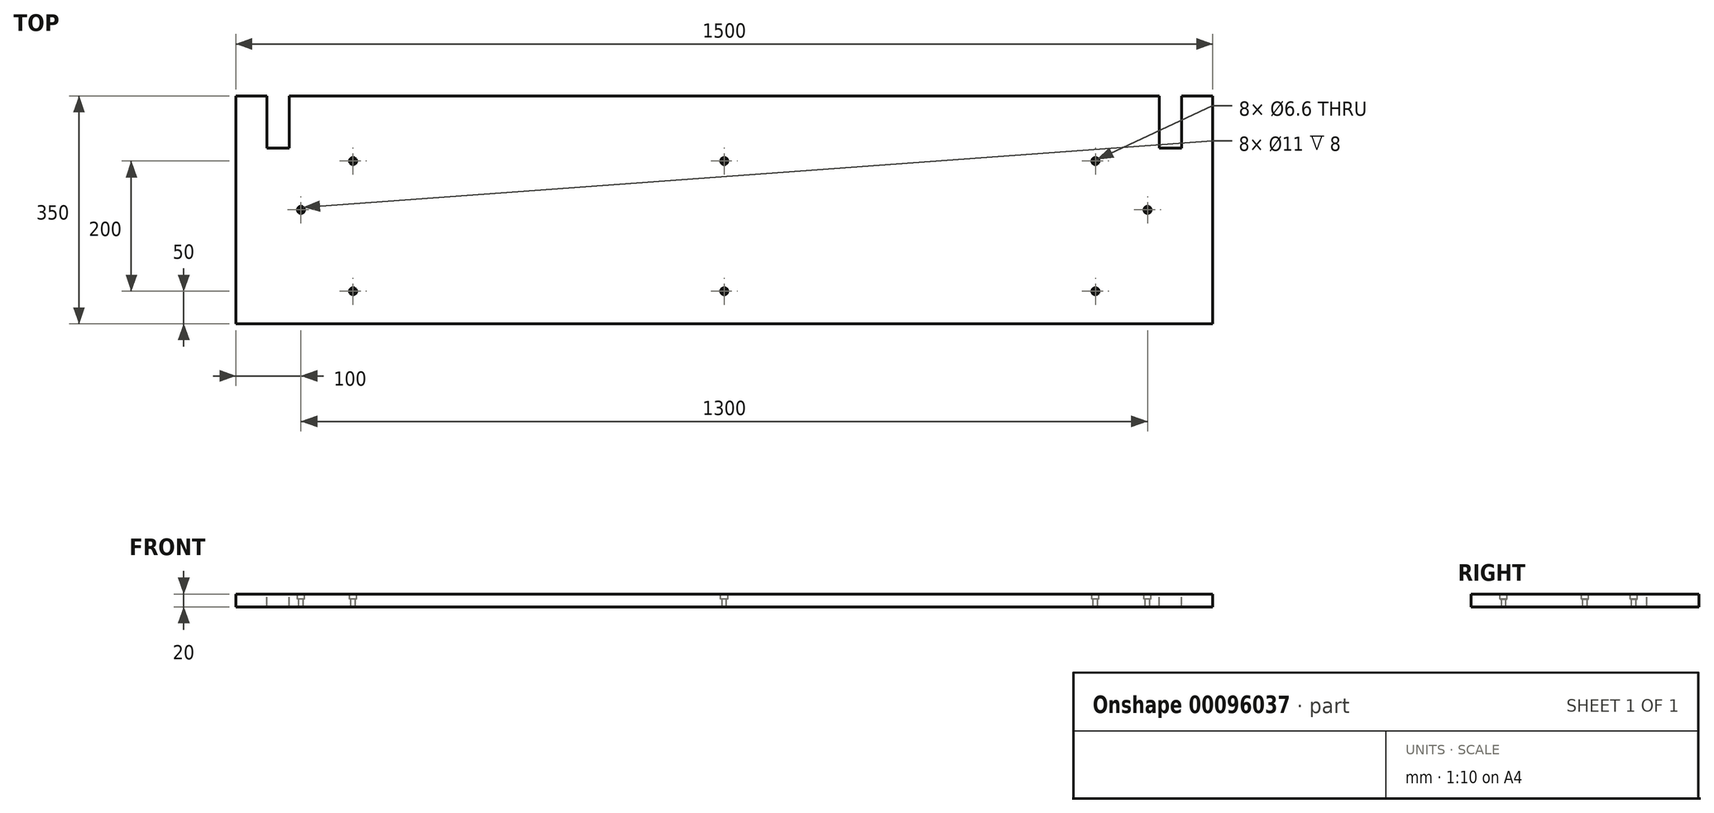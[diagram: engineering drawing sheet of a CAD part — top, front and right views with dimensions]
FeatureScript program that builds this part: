
annotation { "Feature Type Name" : "Feature", "Feature Type Description" : "" }
export const myFeature = defineFeature(function(context is Context, id is Id, definition is map)
    precondition{}
    {
        {
            var Q0;
            Q0=qCreatedBy(makeId("Top.planeOp"),FACE);
            var sketch = newSketch(context, id + "F0", { "sketchPlane" : qUnion([Q0])});
            skLineSegment(sketch, "E0.rect.bottom", {"start": v(750, -175) * mm, "end": v(-750, -175) * mm});
            skLineSegment(sketch, "E0.rect.top", {"start": v(750, 175) * mm, "end": v(-750, 175) * mm});
            skLineSegment(sketch, "E0.rect.left", {"start": v(750, -175) * mm, "end": v(750, 175) * mm});
            skLineSegment(sketch, "E0.rect.right", {"start": v(-750, -175) * mm, "end": v(-750, 175) * mm});
            skPoint(sketch, "E0.rect.middle", {"position": v(0, 0) * mm});
            skSolve(sketch);
        }
        {
            var Q0;
            Q0=qSketchRegion(id+"F0",true);
            extrude(context, id + "F1", {"entities" : qUnion([Q0]), "endBound" : BoundingType.SYMMETRIC, "depth" : 20 * mm});
        }
        {
            var Q0;
            Q0=makeQuery(id+"F1.opExtrude","CAP_FACE",FACE,{"disambiguationData":[OSD([sQuery(id+"F0.wireOp",EDGE,"E0.rect.bottom"),sQuery(id+"F0.wireOp",EDGE,"E0.rect.top"),sQuery(id+"F0.wireOp",EDGE,"E0.rect.left"),sQuery(id+"F0.wireOp",EDGE,"E0.rect.right")])],"isStart":false});
            var sketch = newSketch(context, id + "F2", { "sketchPlane" : qUnion([Q0])});
            skLineSegment(sketch, "E1.bottom", {"start": v(668, 175) * mm, "end": v(702, 175) * mm});
            skLineSegment(sketch, "E1.top", {"start": v(668, 95) * mm, "end": v(702, 95) * mm});
            skLineSegment(sketch, "E1.left", {"start": v(668, 175) * mm, "end": v(668, 95) * mm});
            skLineSegment(sketch, "E1.right", {"start": v(702, 175) * mm, "end": v(702, 95) * mm});
            skLineSegment(sketch, "E2.MirrorCS", {"start": v(-668, 175) * mm, "end": v(-702, 175) * mm});
            skLineSegment(sketch, "E3.MirrorCS", {"start": v(-702, 175) * mm, "end": v(-702, 95) * mm});
            skLineSegment(sketch, "E4.MirrorCS", {"start": v(-668, 95) * mm, "end": v(-702, 95) * mm});
            skLineSegment(sketch, "E5.MirrorCS", {"start": v(-668, 175) * mm, "end": v(-668, 95) * mm});
            skSolve(sketch);
        }
        {
            var Q0;
            Q0 = qSketchRegion(id + "F2", true);
            extrude(context, id + "F3", {"entities" : qUnion([Q0]), "operationType" : NewBodyOperationType.REMOVE, "endBound" : BoundingType.THROUGH_ALL, "oppositeDirection" : true, "depth" : 25 * mm});
        }
        {
            var Q0;
            Q0=makeQuery(id+"F1.opExtrude","CAP_FACE",FACE,{"disambiguationData":[OSD([sQuery(id+"F0.wireOp",EDGE,"E0.rect.bottom"),sQuery(id+"F0.wireOp",EDGE,"E0.rect.top"),sQuery(id+"F0.wireOp",EDGE,"E0.rect.left"),sQuery(id+"F0.wireOp",EDGE,"E0.rect.right")])],"isStart":false});
            var sketch = newSketch(context, id + "F4", { "sketchPlane" : qUnion([Q0])});
            skCircle(sketch, "E6", {"center": v(-570, 75) * mm, "radius": 3.3 * mm});
            skCircle(sketch, "E7", {"center": v(0, 75) * mm, "radius": 3.3 * mm});
            skCircle(sketch, "E8", {"center": v(570, 75) * mm, "radius": 3.3 * mm});
            skCircle(sketch, "E9", {"center": v(-570, -125) * mm, "radius": 3.3 * mm});
            skCircle(sketch, "E10", {"center": v(0, -125) * mm, "radius": 3.3 * mm});
            skCircle(sketch, "E11", {"center": v(570, -125) * mm, "radius": 3.3 * mm});
            skCircle(sketch, "E12", {"center": v(-650, 0) * mm, "radius": 3.3 * mm});
            skCircle(sketch, "E13.MirrorC", {"center": v(650, 0) * mm, "radius": 3.3 * mm});
            skSolve(sketch);
        }
        {
            var Q0;
            Q0 = qSketchRegion(id + "F4", true);
            extrude(context, id + "F5", {"entities" : qUnion([Q0]), "operationType" : NewBodyOperationType.REMOVE, "endBound" : BoundingType.THROUGH_ALL, "oppositeDirection" : true, "depth" : 25 * mm});
        }
        {
            var Q0;
            Q0=makeQuery(id+"F1.opExtrude","CAP_FACE",FACE,{"disambiguationData":[OSD([sQuery(id+"F0.wireOp",EDGE,"E0.rect.bottom"),sQuery(id+"F0.wireOp",EDGE,"E0.rect.top"),sQuery(id+"F0.wireOp",EDGE,"E0.rect.left"),sQuery(id+"F0.wireOp",EDGE,"E0.rect.right")])],"isStart":false});
            var sketch = newSketch(context, id + "F6", { "sketchPlane" : qUnion([Q0])});
            skCircle(sketch, "E14", {"center": v(-570, 75) * mm, "radius": 5.5 * mm});
            skCircle(sketch, "E15", {"center": v(-650, 0) * mm, "radius": 5.5 * mm});
            skCircle(sketch, "E16", {"center": v(-570, -125) * mm, "radius": 5.5 * mm});
            skCircle(sketch, "E17", {"center": v(0, -125) * mm, "radius": 5.5 * mm});
            skCircle(sketch, "E18", {"center": v(570, -125) * mm, "radius": 5.5 * mm});
            skCircle(sketch, "E19", {"center": v(650, 0) * mm, "radius": 5.5 * mm});
            skCircle(sketch, "E20", {"center": v(570, 75) * mm, "radius": 5.5 * mm});
            skCircle(sketch, "E21", {"center": v(0, 75) * mm, "radius": 5.5 * mm});
            skSolve(sketch);
        }
        {
            var Q0;
            Q0 = qSketchRegion(id + "F6", true);
            extrude(context, id + "F7", {"entities" : qUnion([Q0]), "operationType" : NewBodyOperationType.REMOVE, "oppositeDirection" : true, "depth" : 8 * mm});
        }
    });
